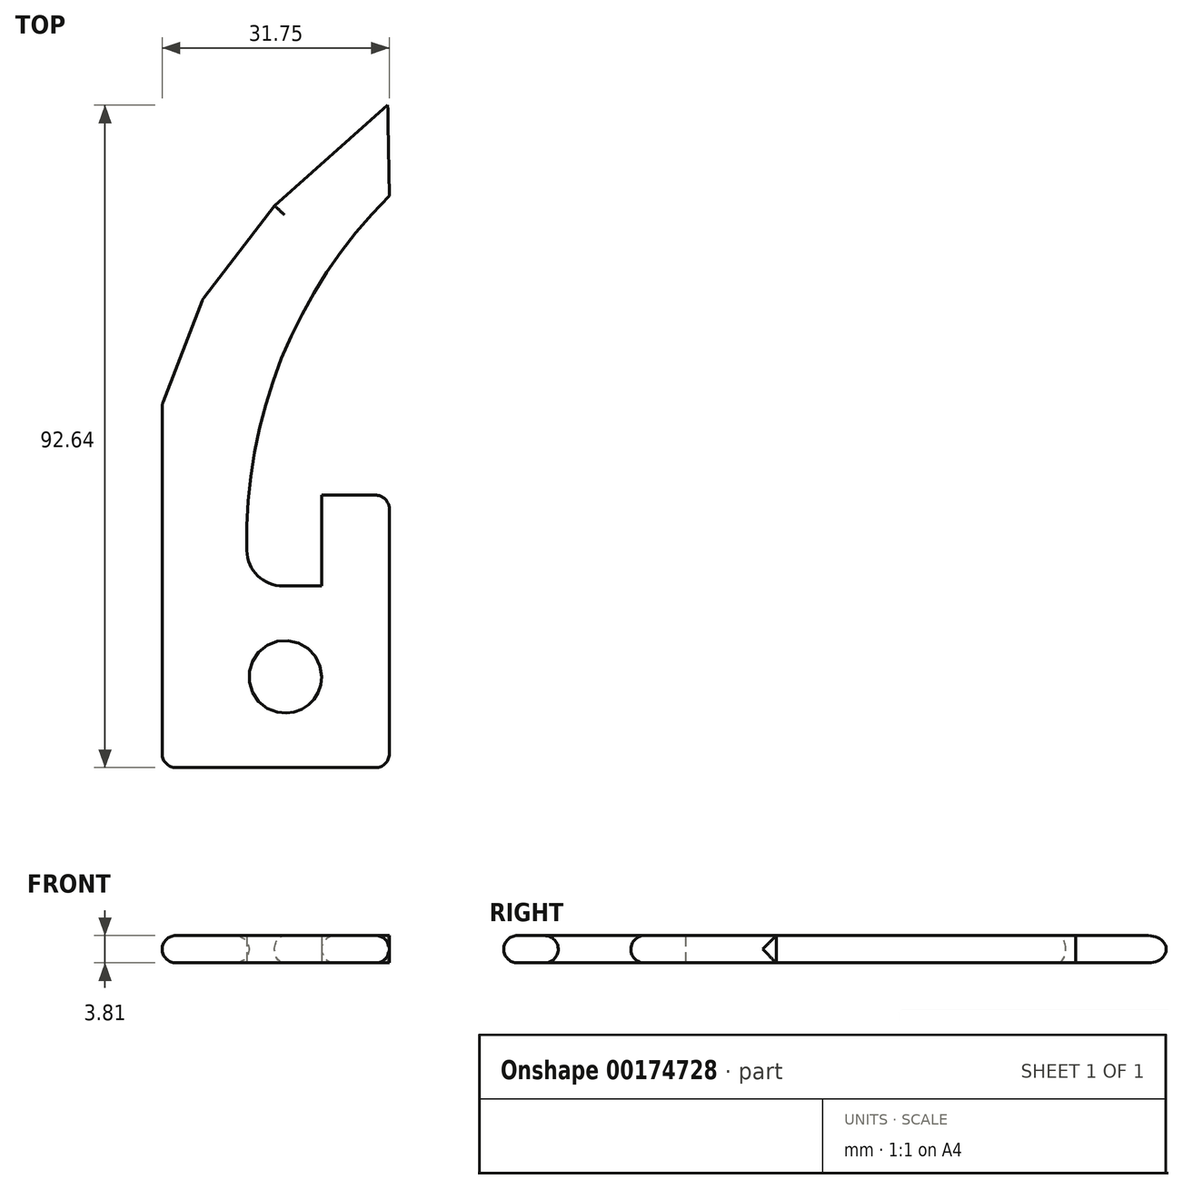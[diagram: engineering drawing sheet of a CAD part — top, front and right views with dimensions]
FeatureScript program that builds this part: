
annotation { "Feature Type Name" : "Feature", "Feature Type Description" : "" }
export const myFeature = defineFeature(function(context is Context, id is Id, definition is map)
    precondition{}
    {
        {
            var Q0;
            Q0=qCreatedBy(makeId("Top.planeOp"),FACE);
            var sketch = newSketch(context, id + "F0", { "sketchPlane" : qUnion([Q0])});
            skLineSegment(sketch, "E0.top", {"start": v(-5.69, -25.4) * mm, "end": v(5.69, -25.4) * mm});
            skLineSegment(sketch, "E0.left", {"start": v(-5.69, 25.4) * mm, "end": v(-5.69, -25.4) * mm});
            skPoint(sketch, "E0.middle", {"position": v(0, 0) * mm});
            skLineSegment(sketch, "E1.bottom", {"start": v(5.69, -25.4) * mm, "end": v(26.06, -25.4) * mm});
            skLineSegment(sketch, "E1.top", {"start": v(6.44, 0) * mm, "end": v(16.6, 0) * mm});
            skLineSegment(sketch, "E1.right", {"start": v(26.06, -25.4) * mm, "end": v(26.06, 0) * mm});
            skLineSegment(sketch, "E2.top", {"start": v(26.06, 12.7) * mm, "end": v(16.6, 12.7) * mm});
            skLineSegment(sketch, "E2.left", {"start": v(26.06, 0) * mm, "end": v(26.06, 12.7) * mm});
            skLineSegment(sketch, "E2.right", {"start": v(16.6, 0) * mm, "end": v(16.6, 12.7) * mm});
            skLineSegment(sketch, "E3", {"start": v(0, 40.13) * mm, "end": v(-5.69, 25.4) * mm});
            skArc(sketch, "E4", {"start": v(26.06, 54.54) * mm, "mid": v(10.1, 29.48) * mm, "end": v(6.44, 0) * mm});
            skPoint(sketch, "E0.bottom.end.orphan", {"position": v(5.69, 25.4) * mm});
            skCircle(sketch, "E5", {"center": v(11.52, -12.7) * mm, "radius": 5.08 * mm});
            skPoint(sketch, "E5.centerSnap0", {"position": v(26.06, -12.7) * mm});
            skPoint(sketch, "E5.centerSnap1", {"position": v(11.52, 0) * mm});
            skLineSegment(sketch, "E6", {"start": v(0, 40.13) * mm, "end": v(10.02, 53.2) * mm});
            skLineSegment(sketch, "E7", {"start": v(10.02, 53.2) * mm, "end": v(25.84, 67.24) * mm});
            skLineSegment(sketch, "E8", {"start": v(25.84, 67.24) * mm, "end": v(26.06, 54.54) * mm});
            skSolve(sketch);
        }
        {
            var Q0;
            Q0=makeQuery(id+"F0.imprint","IMPRINT",FACE,{"disambiguationData":[TD([[makeQuery(id+"F0.imprint","IMPRINT",EDGE,{"derivedFrom":sQuery(id+"F0.wireOp",EDGE,"E0.top")}),1.0]])]});
            extrude(context, id + "F1", {"entities" : qUnion([Q0]), "depth" : 3.8 * mm});
        }
        {
            var Q0;
            Q0=makeQuery(id+"F1.opExtrude","CAP_EDGE",EDGE,{"disambiguationData":[OSD([sQuery(id+"F0.wireOp",EDGE,"E0.left")])],"isStart":false});
            var Q1;
            Q1=makeQuery(id+"F1.opExtrude","CAP_EDGE",EDGE,{"disambiguationData":[OSD([sQuery(id+"F0.wireOp",EDGE,"E0.top"),sQuery(id+"F0.wireOp",EDGE,"E1.bottom")])],"isStart":false});
            var Q2;
            Q2=makeQuery(id+"F1.opExtrude","CAP_EDGE",EDGE,{"disambiguationData":[OSD([sQuery(id+"F0.wireOp",EDGE,"E0.top"),sQuery(id+"F0.wireOp",EDGE,"E1.bottom")])],"isStart":true});
            var Q3;
            Q3=makeQuery(id+"F1.opExtrude","CAP_EDGE",EDGE,{"disambiguationData":[OSD([sQuery(id+"F0.wireOp",EDGE,"E1.right"),sQuery(id+"F0.wireOp",EDGE,"E2.left")])],"isStart":false});
            var Q4;
            Q4=makeQuery(id+"F1.opExtrude","CAP_EDGE",EDGE,{"disambiguationData":[OSD([sQuery(id+"F0.wireOp",EDGE,"E1.right"),sQuery(id+"F0.wireOp",EDGE,"E2.left")])],"isStart":true});
            var Q5;
            Q5=makeQuery(id+"F1.opExtrude","SWEPT_EDGE",EDGE,{"disambiguationData":[OSD([sQuery(id+"F0.wireOp",EDGE,"E1.bottom"),sQuery(id+"F0.wireOp",EDGE,"E1.right")])]});
            var Q6;
            Q6=makeQuery(id+"F1.opExtrude","SWEPT_EDGE",EDGE,{"disambiguationData":[OSD([sQuery(id+"F0.wireOp",EDGE,"E0.top"),sQuery(id+"F0.wireOp",EDGE,"E0.left")])]});
            var Q7;
            Q7=makeQuery(id+"F1.opExtrude","SWEPT_EDGE",EDGE,{"disambiguationData":[OSD([sQuery(id+"F0.wireOp",EDGE,"E2.top"),sQuery(id+"F0.wireOp",EDGE,"E2.left")])]});
            var Q8;
            Q8=makeQuery(id+"F1.opExtrude","SWEPT_EDGE",EDGE,{"disambiguationData":[OSD([sQuery(id+"F0.wireOp",EDGE,"ivynZIt3-clNf-tamm-8hTk-4WhhEsugJnW5"),sQuery(id+"F0.wireOp",EDGE,"E3")])]});
            var Q9;
            Q9=makeQuery(id+"F1.opExtrude","CAP_EDGE",EDGE,{"disambiguationData":[OSD([sQuery(id+"F0.wireOp",EDGE,"E3")])],"isStart":false});
            var Q10;
            Q10=makeQuery(id+"F1.opExtrude","CAP_EDGE",EDGE,{"disambiguationData":[OSD([sQuery(id+"F0.wireOp",EDGE,"E3")])],"isStart":true});
            var Q11;
            Q11=makeQuery(id+"F1.opExtrude","CAP_EDGE",EDGE,{"disambiguationData":[OSD([sQuery(id+"F0.wireOp",EDGE,"E0.left")])],"isStart":true});
            var Q12;
            Q12=makeQuery(id+"F1.opExtrude","CAP_EDGE",EDGE,{"disambiguationData":[OSD([sQuery(id+"F0.wireOp",EDGE,"E5")])],"isStart":true});
            var Q13;
            Q13=makeQuery(id+"F1.opExtrude","CAP_EDGE",EDGE,{"disambiguationData":[OSD([sQuery(id+"F0.wireOp",EDGE,"E5")])],"isStart":false});
            fillet(context, id + "F2", {"entities" : qUnion([Q0, Q1, Q2, Q3, Q4, Q5, Q6, Q7, Q8, Q9, Q10, Q11, Q12, Q13]), "radius" : 1.9 * mm, "tangentPropagation" : true, "allowEdgeOverflow" : false});
        }
        {
            var Q0;
            Q0=makeQuery(id+"F1.opExtrude","CAP_EDGE",EDGE,{"disambiguationData":[OSD([sQuery(id+"F0.wireOp",EDGE,"E6")])],"isStart":false});
            var Q1;
            Q1=makeQuery(id+"F1.opExtrude","CAP_EDGE",EDGE,{"disambiguationData":[OSD([sQuery(id+"F0.wireOp",EDGE,"E6")])],"isStart":true});
            var Q2;
            Q2=makeQuery(id+"F2.opFillet","BLEND_EDGE",EDGE,{"blendedFrom":[makeQuery(id+"F1.opExtrude","CAP_EDGE",EDGE,{"disambiguationData":[OSD([sQuery(id+"F0.wireOp",EDGE,"E3")])],"isStart":false}),makeQuery(id+"F1.opExtrude","SWEPT_FACE",FACE,{"disambiguationData":[OSD([sQuery(id+"F0.wireOp",EDGE,"E6")])]})],"blendedInto":[makeQuery(id+"F1.opExtrude","SWEPT_FACE",FACE,{"disambiguationData":[OSD([sQuery(id+"F0.wireOp",EDGE,"E6")])]})]});
            var Q3;
            Q3=makeQuery(id+"F2.opFillet","BLEND_EDGE",EDGE,{"blendedFrom":[makeQuery(id+"F1.opExtrude","CAP_EDGE",EDGE,{"disambiguationData":[OSD([sQuery(id+"F0.wireOp",EDGE,"E3")])],"isStart":true}),makeQuery(id+"F1.opExtrude","SWEPT_FACE",FACE,{"disambiguationData":[OSD([sQuery(id+"F0.wireOp",EDGE,"E6")])]})],"blendedInto":[makeQuery(id+"F1.opExtrude","SWEPT_FACE",FACE,{"disambiguationData":[OSD([sQuery(id+"F0.wireOp",EDGE,"E6")])]})]});
            var Q4;
            Q4=makeQuery(id+"F1.opExtrude","CAP_EDGE",EDGE,{"disambiguationData":[OSD([sQuery(id+"F0.wireOp",EDGE,"E7")])],"isStart":false});
            var Q5;
            Q5=makeQuery(id+"F1.opExtrude","CAP_EDGE",EDGE,{"disambiguationData":[OSD([sQuery(id+"F0.wireOp",EDGE,"E7")])],"isStart":true});
            fillet(context, id + "F3", {"entities" : qUnion([Q0, Q1, Q2, Q3, Q4, Q5]), "radius" : 1.9 * mm, "tangentPropagation" : true, "allowEdgeOverflow" : false});
        }
        {
            var Q0;
            Q0=makeQuery(id+"F1.opExtrude","SWEPT_EDGE",EDGE,{"disambiguationData":[OSD([sQuery(id+"F0.wireOp",EDGE,"E1.top"),sQuery(id+"F0.wireOp",EDGE,"E4")])]});
            fillet(context, id + "F4", {"entities" : qUnion([Q0]), "radius" : 5.08 * mm, "tangentPropagation" : true, "allowEdgeOverflow" : false});
        }
    });
